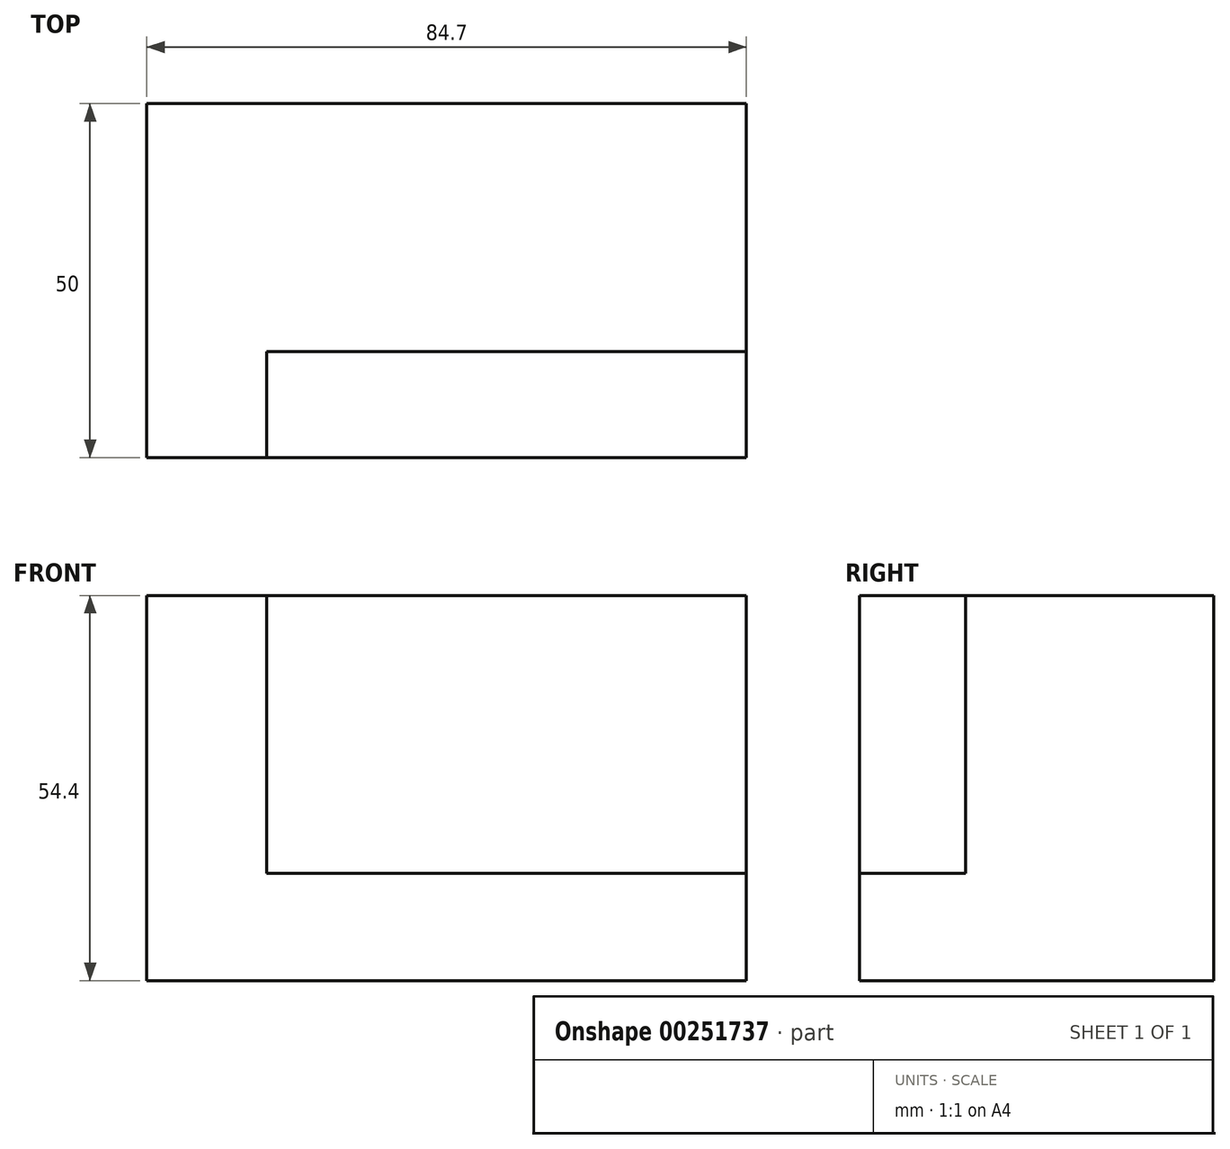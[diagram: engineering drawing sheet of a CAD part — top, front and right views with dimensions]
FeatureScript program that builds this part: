
annotation { "Feature Type Name" : "Feature", "Feature Type Description" : "" }
export const myFeature = defineFeature(function(context is Context, id is Id, definition is map)
    precondition{}
    {
        {
            var Q0;
            Q0=qCreatedBy(makeId("Front.planeOp"),FACE);
            var sketch = newSketch(context, id + "F0", { "sketchPlane" : qUnion([Q0])});
            skLineSegment(sketch, "E0.bottom", {"start": v(-42.35, -27.2) * mm, "end": v(42.35, -27.2) * mm});
            skLineSegment(sketch, "E0.top", {"start": v(-42.35, 27.2) * mm, "end": v(42.35, 27.2) * mm});
            skLineSegment(sketch, "E0.left", {"start": v(-42.35, -27.2) * mm, "end": v(-42.35, 27.2) * mm});
            skLineSegment(sketch, "E0.right", {"start": v(42.35, -27.2) * mm, "end": v(42.35, 27.2) * mm});
            skPoint(sketch, "E0.middle", {"position": v(0, 0) * mm});
            skSolve(sketch);
        }
        {
            var Q0;
            Q0 = qSketchRegion(id + "F0", true);
            extrude(context, id + "F1", {"entities" : qUnion([Q0]), "oppositeDirection" : true, "depth" : 50 * mm});
        }
        {
            var Q0;
            Q0=qCreatedBy(makeId("Front.planeOp"),FACE);
            var sketch = newSketch(context, id + "F2", { "sketchPlane" : qUnion([Q0])});
            skLineSegment(sketch, "E1", {"start": v(-25.41, 27.2) * mm, "end": v(-25.41, 9.8) * mm});
            skLineSegment(sketch, "E2", {"start": v(-25.41, 9.8) * mm, "end": v(-25.41, -12.04) * mm});
            skLineSegment(sketch, "E3", {"start": v(-25.41, -12.04) * mm, "end": v(42.35, -12.04) * mm});
            skLineSegment(sketch, "E4.0", {"start": v(42.35, 27.2) * mm, "end": v(-25.41, 27.2) * mm});
            skLineSegment(sketch, "E5.0", {"start": v(42.35, 27.2) * mm, "end": v(42.35, -12.04) * mm});
            skPoint(sketch, "E6.orphan", {"position": v(-42.35, 27.2) * mm});
            skPoint(sketch, "E7.orphan", {"position": v(42.35, -27.2) * mm});
            skSolve(sketch);
        }
        {
            var Q0;
            Q0 = qSketchRegion(id + "F2", true);
            extrude(context, id + "F3", {"entities" : qUnion([Q0]), "operationType" : NewBodyOperationType.REMOVE, "oppositeDirection" : true, "depth" : 15 * mm});
        }
    });
